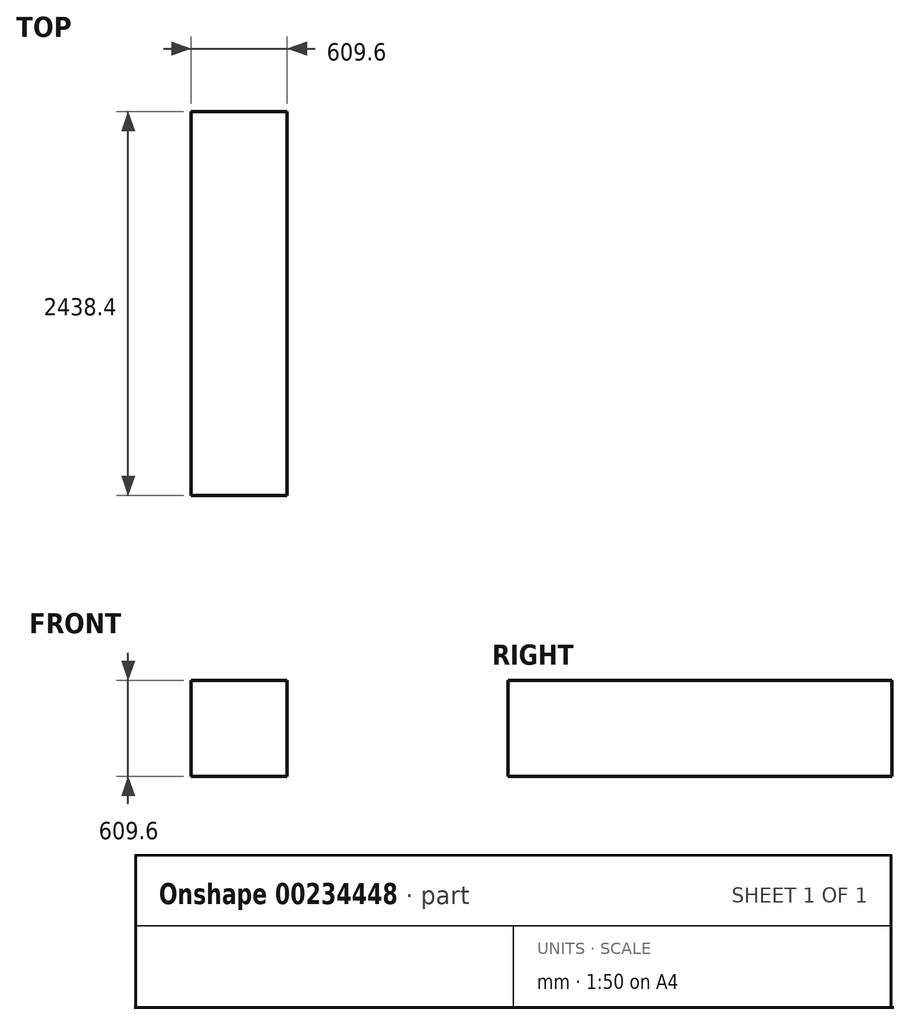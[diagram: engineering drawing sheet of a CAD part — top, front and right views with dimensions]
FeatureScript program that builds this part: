
annotation { "Feature Type Name" : "Feature", "Feature Type Description" : "" }
export const myFeature = defineFeature(function(context is Context, id is Id, definition is map)
    precondition{}
    {
        {
            var Q0;
            Q0=qCreatedBy(makeId("Front.planeOp"),FACE);
            var sketch = newSketch(context, id + "F0", { "sketchPlane" : qUnion([Q0])});
            skLineSegment(sketch, "E0.bottom", {"start": v(0, 0) * mm, "end": v(609.6, 0) * mm});
            skLineSegment(sketch, "E0.top", {"start": v(0, 609.6) * mm, "end": v(609.6, 609.6) * mm});
            skLineSegment(sketch, "E0.left", {"start": v(0, 0) * mm, "end": v(0, 609.6) * mm});
            skLineSegment(sketch, "E0.right", {"start": v(609.6, 0) * mm, "end": v(609.6, 609.6) * mm});
            skSolve(sketch);
        }
        {
            var Q0;
            Q0=makeQuery(id+"F0.imprint","IMPRINT",FACE,{"disambiguationData":[TD([[makeQuery(id+"F0.imprint","IMPRINT",EDGE,{"derivedFrom":sQuery(id+"F0.wireOp",EDGE,"E0.bottom")}),1.0]])]});
            extrude(context, id + "F1", {"entities" : qUnion([Q0]), "depth" : 2438.4 * mm});
        }
    });
